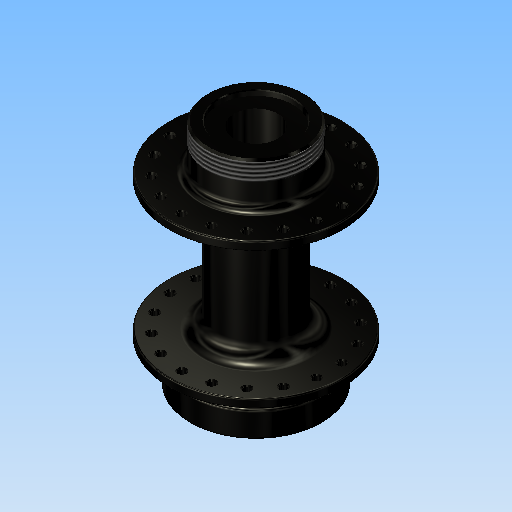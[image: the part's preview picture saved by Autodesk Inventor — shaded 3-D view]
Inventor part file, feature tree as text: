
AUTODESK INVENTOR PART (.ipt)
format: ipt  version: 2018 (Build 220112000, 112)  size: 512,512 bytes
history: native  units: mm
features: chamfer x6, fillet x6, sketch x5, extrude x4, pattern_circular x2, revolve x1, hole x1, direct_edit x1, thread x1, move_body x1
ambient origin geometry x8: Origin, YZ Plane, XZ Plane, XY Plane, X Axis, Y Axis, Z Axis, Center Point
bodies: Solid2 (feature_tree)
feature tree (28):
  revolve  "Revolution1"  [1 undecoded]
  chamfer  "Chamfer1"  Distance=3.42mm
  fillet  "Fillet1"  Radius=6.0mm
  extrude  "Extrusion2"  Depth=26.0mm
  chamfer  "Chamfer2"  Distance=19.58mm
  pattern_circular  "Circular Pattern1"  [2 undecoded]
  extrude  "Extrusion3"  TaperAngle=90.0deg  [1 undecoded]
  chamfer  "Chamfer3"  Distance=10.0mm Angle=45.0deg
  pattern_circular  "Circular Pattern2"  [2 undecoded]
  extrude  "Extrusion4"  Depth=2.0mm
  fillet  "Fillet2"  Radius=5.0mm
  fillet  "Fillet3"  [1 undecoded]
  fillet  "Fillet4"  Radius=2.0mm
  fillet  "Fillet5"  Radius=180.0mm
  extrude  "Extrusion5"  Depth=2.0mm
  hole  "Hole1"  [1 undecoded]
  chamfer  "Chamfer5"  Distance=10.0mm
  chamfer  "Chamfer6"  Distance=2.0mm Angle=45.0deg
  direct_edit  "Direct Edit1"
  fillet  "Fillet6"  Radius=60.0mm
  thread  "Thread1"  [1 undecoded]
  chamfer  "Chamfer7"  Distance=29.0mm
  sketch  "Sketch1"  dims[d3=15.0mm d4=49.8mm]
  sketch  "Sketch4"  dims[d5=34.0mm]
  sketch  "Sketch5"  dims[d6=34.0mm]
  sketch  "Sketch6"  dims[d7=21.5mm]
  sketch  "Sketch7"  dims[d8=3.42mm d9=3.42mm d10=6.0mm d11=26.0mm d12=19.58mm d13=17.5mm d14=90.0deg d15=10.0mm d16=2.0mm d17=45.0deg d18=4.0mm d19=2.7mm d21=5.0mm d22=0.0mm d23=0.0mm d24=0.5mm d25=2.0mm d26=45.0deg d27=180.0mm d28=360.0deg d30=4.01mm d31=4.0mm d32=10.0mm d33=0.0mm d34=0.5mm d35=2.0mm d36=45.0deg d37=60.0mm d38=360.0deg d40=38.0mm d41=29.0mm d42=17.0mm d43=0.0mm d47=6.0mm d48=2.0mm d49=1.0mm d50=0.6mm d51=32.8mm d52=29.0mm d53=2.0mm d54=0.0mm d79=10.0mm d80=10.0mm d57=17.0mm d58=6.0mm d59=4.0mm d60=2.0mm d61=90.0deg d62=8.0mm d63=20.594885mm d64=0.3mm d65=2.0mm d66=45.0deg d67=0.3mm d68=2.0mm d69=45.0deg d70=0.0mm d71=0.0mm d72=15.0mm d73=3.0mm d74=7.6mm d75=0.0mm d76=0.7mm d77=2.0mm d78=45.0deg]
  move_body  "Move1"
note: 9 required parameter values undecoded (feature->parameter linkage not recoverable at this tier; creation-order binding heuristic only, values carry confidence <= 0.55)